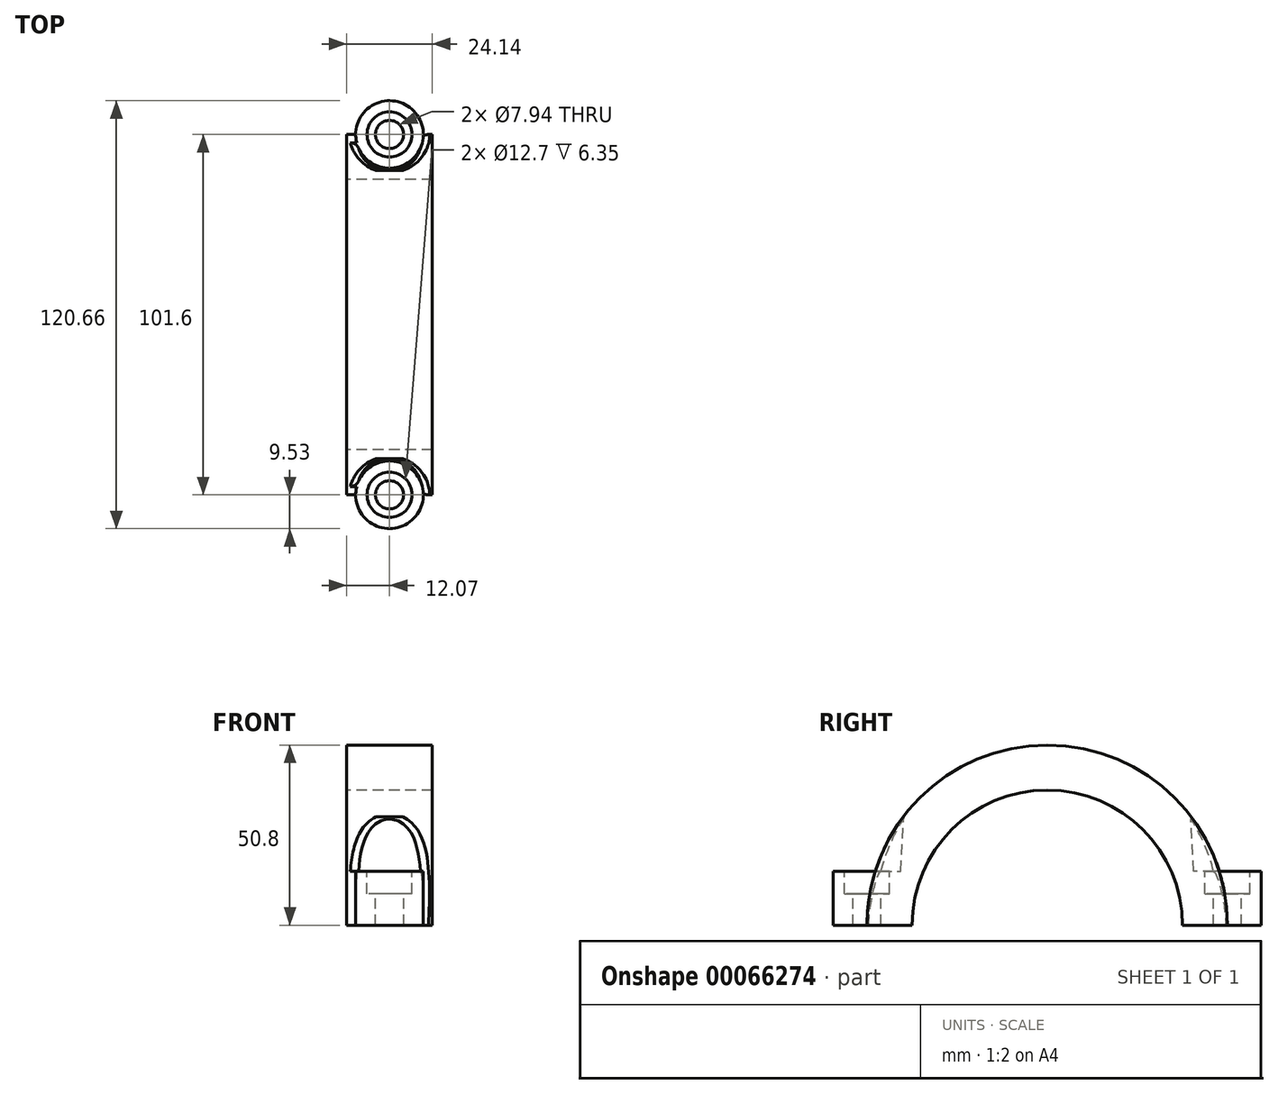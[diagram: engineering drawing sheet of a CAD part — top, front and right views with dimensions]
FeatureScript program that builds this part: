
annotation { "Feature Type Name" : "Feature", "Feature Type Description" : "" }
export const myFeature = defineFeature(function(context is Context, id is Id, definition is map)
    precondition{}
    {
        {
            var Q0;
            Q0=qCreatedBy(makeId("Right.planeOp"),FACE);
            var sketch = newSketch(context, id + "F0", { "sketchPlane" : qUnion([Q0])});
            skArc(sketch, "E0", {"start": v(38.1, 0) * mm, "mid": v(0, 38.1) * mm, "end": v(-38.1, 0) * mm});
            skArc(sketch, "E1.0", {"start": v(50.8, 0) * mm, "mid": v(0, 50.8) * mm, "end": v(-50.8, 0) * mm});
            skLineSegment(sketch, "E2.trimOffspring", {"start": v(38.1, 0) * mm, "end": v(50.8, 0) * mm});
            skLineSegment(sketch, "E3", {"start": v(-50.8, 0) * mm, "end": v(-38.1, 0) * mm});
            skSolve(sketch);
        }
        {
            var Q0;
            Q0 = qSketchRegion(id + "F0", true);
            extrude(context, id + "F1", {"entities" : qUnion([Q0]), "endBound" : BoundingType.SYMMETRIC, "depth" : 24.13 * mm});
        }
        {
            var Q0;
            Q0=makeQuery(id+"F1.opExtrude","SWEPT_FACE",FACE,{"disambiguationData":[OSD([sQuery(id+"F0.wireOp",EDGE,"E3")])]});
            var sketch = newSketch(context, id + "F2", { "sketchPlane" : qUnion([Q0])});
            skCircle(sketch, "E4", {"center": v(0, -50.8) * mm, "radius": 9.53 * mm});
            skCircle(sketch, "E5", {"center": v(0, 50.8) * mm, "radius": 9.53 * mm});
            skSolve(sketch);
        }
        {
            var Q0;
            Q0 = qSketchRegion(id + "F2", true);
            extrude(context, id + "F3", {"entities" : qUnion([Q0]), "operationType" : NewBodyOperationType.ADD, "oppositeDirection" : true, "depth" : 15.25 * mm});
        }
        {
            var Q0;
            Q0=makeQuery(id+"F3.opExtrude","CAP_FACE",FACE,{"disambiguationData":[OSD([sQuery(id+"F2.wireOp",EDGE,"E5")])],"isStart":false});
            var sketch = newSketch(context, id + "F4", { "sketchPlane" : qUnion([Q0])});
            skCircle(sketch, "E6", {"center": v(0, 50.8) * mm, "radius": 9.53 * mm});
            skCircle(sketch, "E7", {"center": v(0, -50.8) * mm, "radius": 9.53 * mm});
            skSolve(sketch);
        }
        {
            var Q0;
            Q0 = qSketchRegion(id + "F4", true);
            extrude(context, id + "F5", {"entities" : qUnion([Q0]), "operationType" : NewBodyOperationType.REMOVE, "depth" : 15.25 * mm, "hasDraft" : true, "draftAngle" : 3 * degree});
        }
        {
            var Q0;
            Q0=makeQuery(id+"F5.boolean.opBoolean","MERGE",FACE,{"derivedFrom":[makeQuery(id+"F3.opExtrude","CAP_FACE",FACE,{"disambiguationData":[OSD([sQuery(id+"F2.wireOp",EDGE,"E4")])],"isStart":false}),makeQuery(id+"F5.opExtrude","CAP_FACE",FACE,{"disambiguationData":[OSD([sQuery(id+"F4.wireOp",EDGE,"E6")])],"isStart":true})]});
            var sketch = newSketch(context, id + "F6", { "sketchPlane" : qUnion([Q0])});
            skPoint(sketch, "E8", {"position": v(0, 50.8) * mm});
            skPoint(sketch, "E9", {"position": v(0, -50.8) * mm});
            skSolve(sketch);
        }
        {
            var Q0;
            Q0=makeQuery(id+"F5.boolean.opBoolean","INTERSECT",EDGE,{"disambiguationData":[OD(1.0)],"derivedFrom":[makeQuery(id+"F1.opExtrude","SWEPT_FACE",FACE,{"disambiguationData":[OSD([sQuery(id+"F0.wireOp",EDGE,"E1.0")])]}),makeQuery(id+"F5.opExtrude","SWEPT_FACE",FACE,{"disambiguationData":[OSD([sQuery(id+"F4.wireOp",EDGE,"E7")])]})]});
            fillet(context, id + "F7", {"entities" : qUnion([Q0]), "radius" : 2.54 * mm, "tangentPropagation" : true, "allowEdgeOverflow" : false});
        }
        {
            var Q0;
            Q0=makeQuery(id+"F5.boolean.opBoolean","INTERSECT",EDGE,{"disambiguationData":[OD(1.0)],"derivedFrom":[makeQuery(id+"F1.opExtrude","SWEPT_FACE",FACE,{"disambiguationData":[OSD([sQuery(id+"F0.wireOp",EDGE,"E1.0")])]}),makeQuery(id+"F5.opExtrude","SWEPT_FACE",FACE,{"disambiguationData":[OSD([sQuery(id+"F4.wireOp",EDGE,"E6")])]})]});
            fillet(context, id + "F8", {"entities" : qUnion([Q0]), "radius" : 2.54 * mm, "tangentPropagation" : true, "allowEdgeOverflow" : false});
        }
        {
            var Q0;
            Q0=sQuery(id+"F6.wireOp",VERTEX,"E8");
            var Q1;
            Q1=sQuery(id+"F6.wireOp",VERTEX,"E9");
            var Q2;
            Q2=makeQuery(id+"F1.opExtrude","SWEPT_BODY",BODY,{"disambiguationData":[OSD([sQuery(id+"F0.wireOp",EDGE,"E0"),sQuery(id+"F0.wireOp",EDGE,"E1.0"),sQuery(id+"F0.wireOp",EDGE,"E2.trimOffspring"),sQuery(id+"F0.wireOp",EDGE,"E3")])]});
            hole(context, id + "F9", {"style" : HoleStyle.C_BORE, "holeDiameter" : 7.94 * mm, "cBoreDiameter" : 12.7 * mm, "cBoreDepth" : 6.35 * mm, "endStyle" : HoleEndStyle.THROUGH, "locations" : qUnion([Q0, Q1]), "scope" : qUnion([Q2])});
        }
    });
